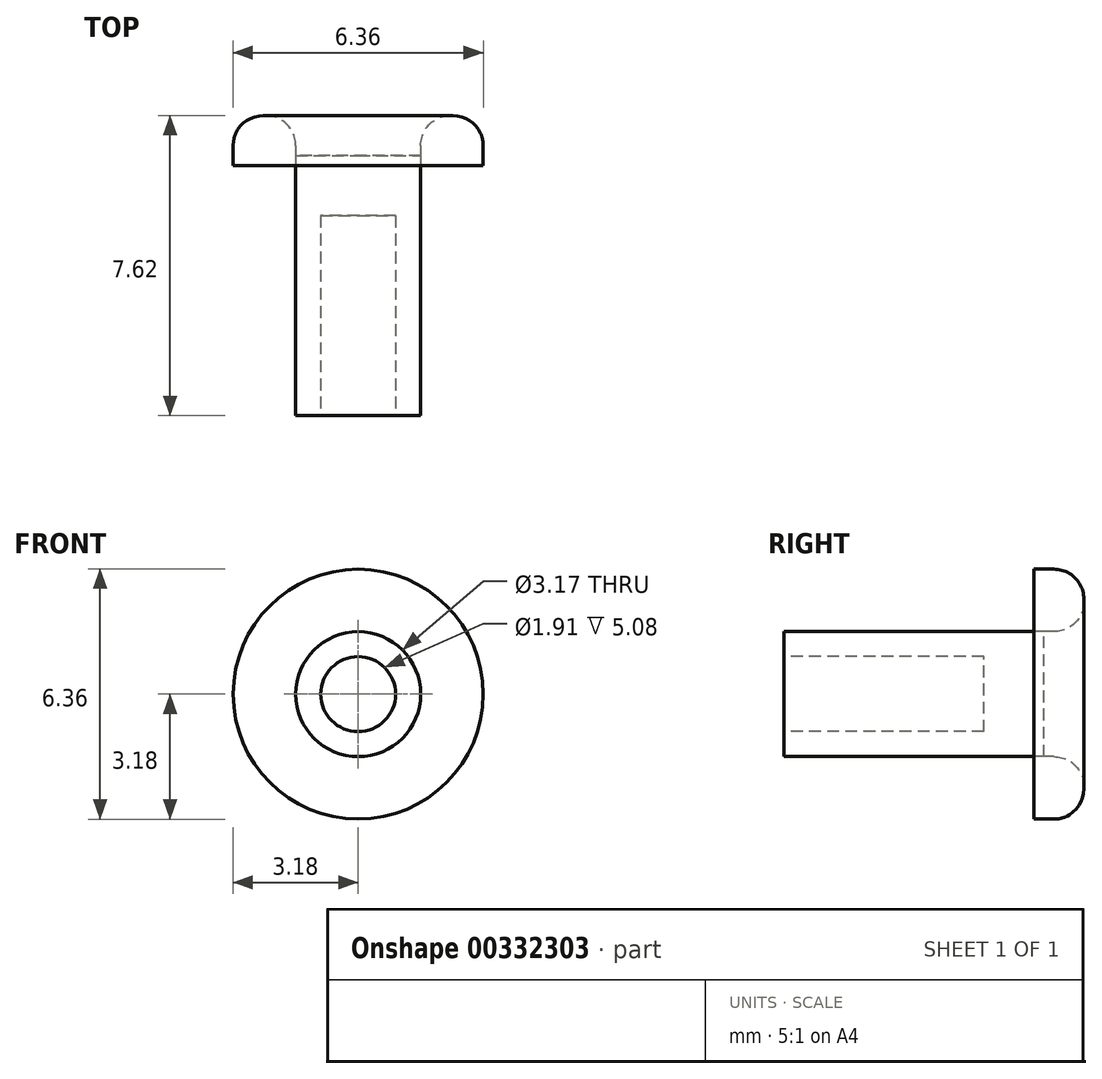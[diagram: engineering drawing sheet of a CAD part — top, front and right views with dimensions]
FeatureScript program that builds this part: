
annotation { "Feature Type Name" : "Feature", "Feature Type Description" : "" }
export const myFeature = defineFeature(function(context is Context, id is Id, definition is map)
    precondition{}
    {
        {
            var Q0;
            Q0=qCreatedBy(makeId("Front.planeOp"),FACE);
            var sketch = newSketch(context, id + "F0", { "sketchPlane" : qUnion([Q0])});
            skCircle(sketch, "E0", {"center": v(0, 0) * mm, "radius": 1.59 * mm});
            skSolve(sketch);
        }
        {
            var Q0;
            Q0=makeQuery(id+"F0.imprint","IMPRINT",FACE,{"disambiguationData":[TD([[makeQuery(id+"F0.imprint","IMPRINT",EDGE,{"derivedFrom":sQuery(id+"F0.wireOp",EDGE,"E0")}),1.0]])]});
            extrude(context, id + "F1", {"entities" : qUnion([Q0]), "depth" : 6.35 * mm});
        }
        {
            var Q0;
            Q0=makeQuery(id+"F1.opExtrude","CAP_FACE",FACE,{"disambiguationData":[OSD([sQuery(id+"F0.wireOp",EDGE,"E0")])],"isStart":false});
            var sketch = newSketch(context, id + "F2", { "sketchPlane" : qUnion([Q0])});
            skCircle(sketch, "E1", {"center": v(0, 0) * mm, "radius": 0.95 * mm});
            skSolve(sketch);
        }
        {
            var Q0;
            Q0=qSketchRegion(id+"F2",true);
            extrude(context, id + "F3", {"entities" : qUnion([Q0]), "operationType" : NewBodyOperationType.REMOVE, "oppositeDirection" : true, "depth" : 5.08 * mm});
        }
        {
            var Q0;
            Q0=makeQuery(id+"F1.opExtrude","CAP_FACE",FACE,{"disambiguationData":[OSD([sQuery(id+"F0.wireOp",EDGE,"E0")])],"isStart":true});
            var sketch = newSketch(context, id + "F4", { "sketchPlane" : qUnion([Q0])});
            skCircle(sketch, "E2", {"center": v(0, 0) * mm, "radius": 3.18 * mm});
            skSolve(sketch);
        }
        {
            var Q0;
            Q0=makeQuery(id+"F4.imprint","IMPRINT",FACE,{"disambiguationData":[TD([[makeQuery(id+"F4.imprint","IMPRINT",EDGE,{"derivedFrom":sQuery(id+"F4.wireOp",EDGE,"E2")}),1.0]])]});
            extrude(context, id + "F5", {"entities" : qUnion([Q0]), "depth" : 1.27 * mm});
        }
        {
            var Q0;
            Q0=makeQuery(id+"F5.opExtrude","CAP_EDGE",EDGE,{"disambiguationData":[OSD([sQuery(id+"F4.wireOp",EDGE,"E2")])],"isStart":false});
            var Q1;
            Q1=makeQuery(id+"F5.opExtrude","CAP_EDGE",EDGE,{"disambiguationData":[OSD([sQuery(id+"F0.wireOp",EDGE,"E0")])],"isStart":false});
            fillet(context, id + "F6", {"entities" : qUnion([Q0, Q1]), "radius" : 0.76 * mm, "tangentPropagation" : true, "allowEdgeOverflow" : false});
        }
        {
            var Q0;
            Q0=makeQuery(id+"F1.opExtrude","CAP_FACE",FACE,{"disambiguationData":[OSD([sQuery(id+"F0.wireOp",EDGE,"E0")])],"isStart":true});
            extrude(context, id + "F7", {"entities" : qUnion([Q0]), "depth" : 0.25 * mm});
        }
    });
